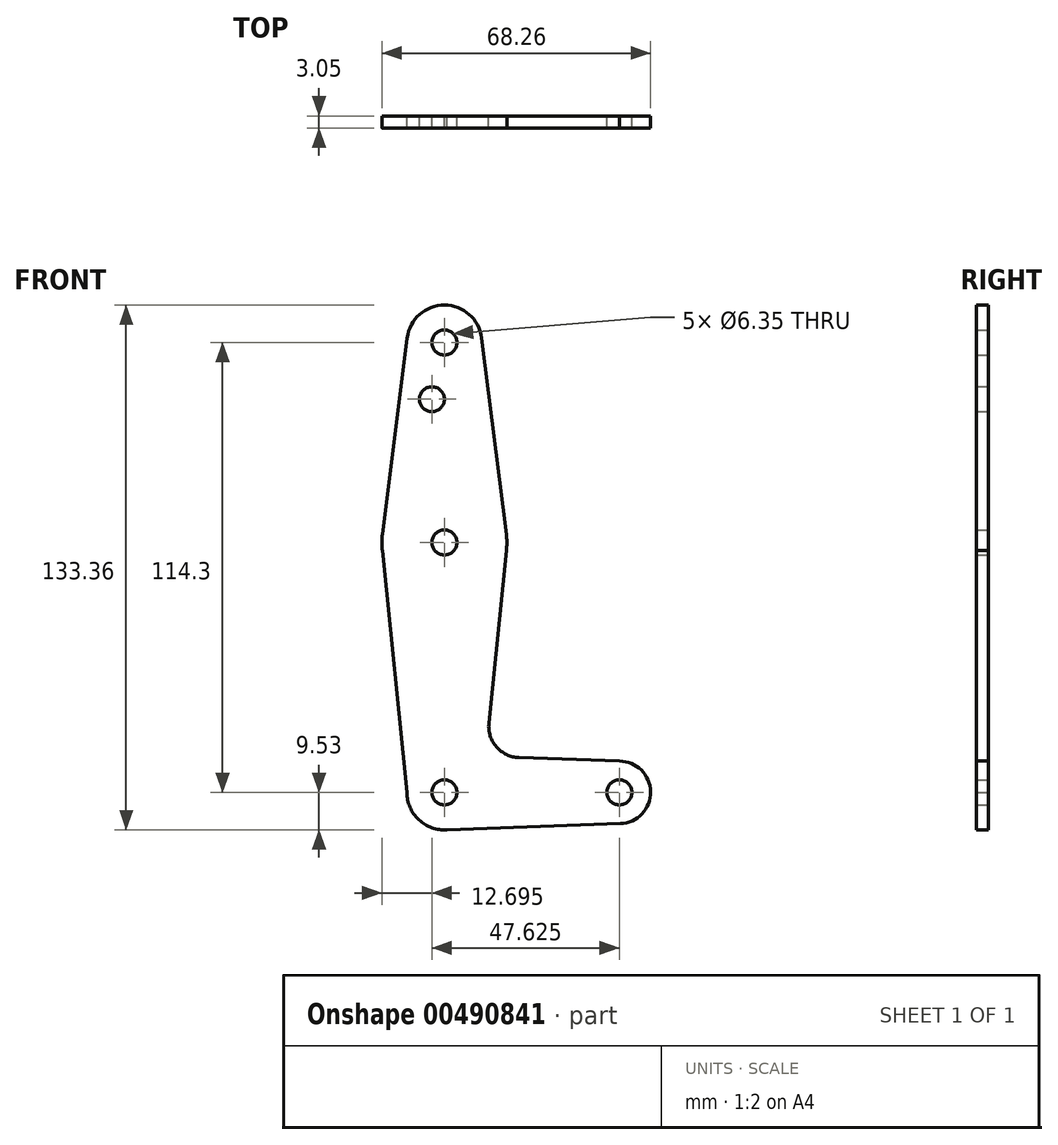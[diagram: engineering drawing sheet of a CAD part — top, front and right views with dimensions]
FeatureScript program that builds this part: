
annotation { "Feature Type Name" : "Feature", "Feature Type Description" : "" }
export const myFeature = defineFeature(function(context is Context, id is Id, definition is map)
    precondition{}
    {
        {
            var Q0;
            Q0=qCreatedBy(makeId("Front.planeOp"),FACE);
            var sketch = newSketch(context, id + "F0", { "sketchPlane" : qUnion([Q0])});
            skLineSegment(sketch, "E0", {"start": v(0, 114.3) * mm, "end": v(0, 0) * mm});
            skLineSegment(sketch, "E1", {"start": v(0, 0) * mm, "end": v(44.45, 0) * mm});
            skCircle(sketch, "E2", {"center": v(0, 114.3) * mm, "radius": 9.53 * mm});
            skCircle(sketch, "E3", {"center": v(0, 63.5) * mm, "radius": 15.88 * mm});
            skCircle(sketch, "E4", {"center": v(0, 0) * mm, "radius": 9.53 * mm});
            skCircle(sketch, "E5", {"center": v(44.45, 0) * mm, "radius": 7.94 * mm});
            skLineSegment(sketch, "E6", {"start": v(15.75, 65.48) * mm, "end": v(9.45, 115.5) * mm});
            skLineSegment(sketch, "E7", {"start": v(-15.75, 65.48) * mm, "end": v(-9.45, 115.5) * mm});
            skLineSegment(sketch, "E8", {"start": v(0, -9.53) * mm, "end": v(44.73, -7.93) * mm});
            skCircle(sketch, "E9", {"center": v(0, 114.3) * mm, "radius": 3.18 * mm});
            skCircle(sketch, "E10", {"center": v(0, 0) * mm, "radius": 3.18 * mm});
            skCircle(sketch, "E11", {"center": v(44.45, 0) * mm, "radius": 3.18 * mm});
            skCircle(sketch, "E12", {"center": v(-3.17, 99.89) * mm, "radius": 3.18 * mm});
            skLineSegment(sketch, "E13", {"start": v(-9.52, 0) * mm, "end": v(-15.75, 61.52) * mm});
            skCircle(sketch, "E14", {"center": v(0, 63.5) * mm, "radius": 3.18 * mm});
            skLineSegment(sketch, "E15", {"start": v(15.75, 61.52) * mm, "end": v(11.3, 17.6) * mm});
            skLineSegment(sketch, "E16", {"start": v(18.93, 8.85) * mm, "end": v(44.45, 7.94) * mm});
            skPoint(sketch, "E17.newPointB", {"position": v(0, 9.52) * mm});
            skArc(sketch, "E17.filletArc", {"start": v(11.3, 17.6) * mm, "mid": v(13.22, 11.57) * mm, "end": v(18.93, 8.85) * mm});
            skSolve(sketch);
        }
        {
            var Q0;
            Q0 = qSketchRegion(id + "F0", true);
            var Q1;
            {var subQ0=sQuery(id+"F0.wireOp",EDGE,"E4");var subQ1=sQuery(id+"F0.wireOp",EDGE,"E0");var subQ2=makeQuery(id+"F0.imprint","INTERSECT",VERTEX,{"derivedFrom":[subQ1,subQ0]});Q1=makeQuery(id+"F0.imprint","IMPRINT",FACE,{"disambiguationData":[TD([[makeQuery(id+"F0.imprint","IMPRINT",EDGE,{"disambiguationData":[TD([[subQ2,-1.0]])],"derivedFrom":subQ1}),1.0]])]});}
            extrude(context, id + "F1", {"entities" : qUnion([Q0, Q1]), "depth" : 3.05 * mm});
        }
    });
